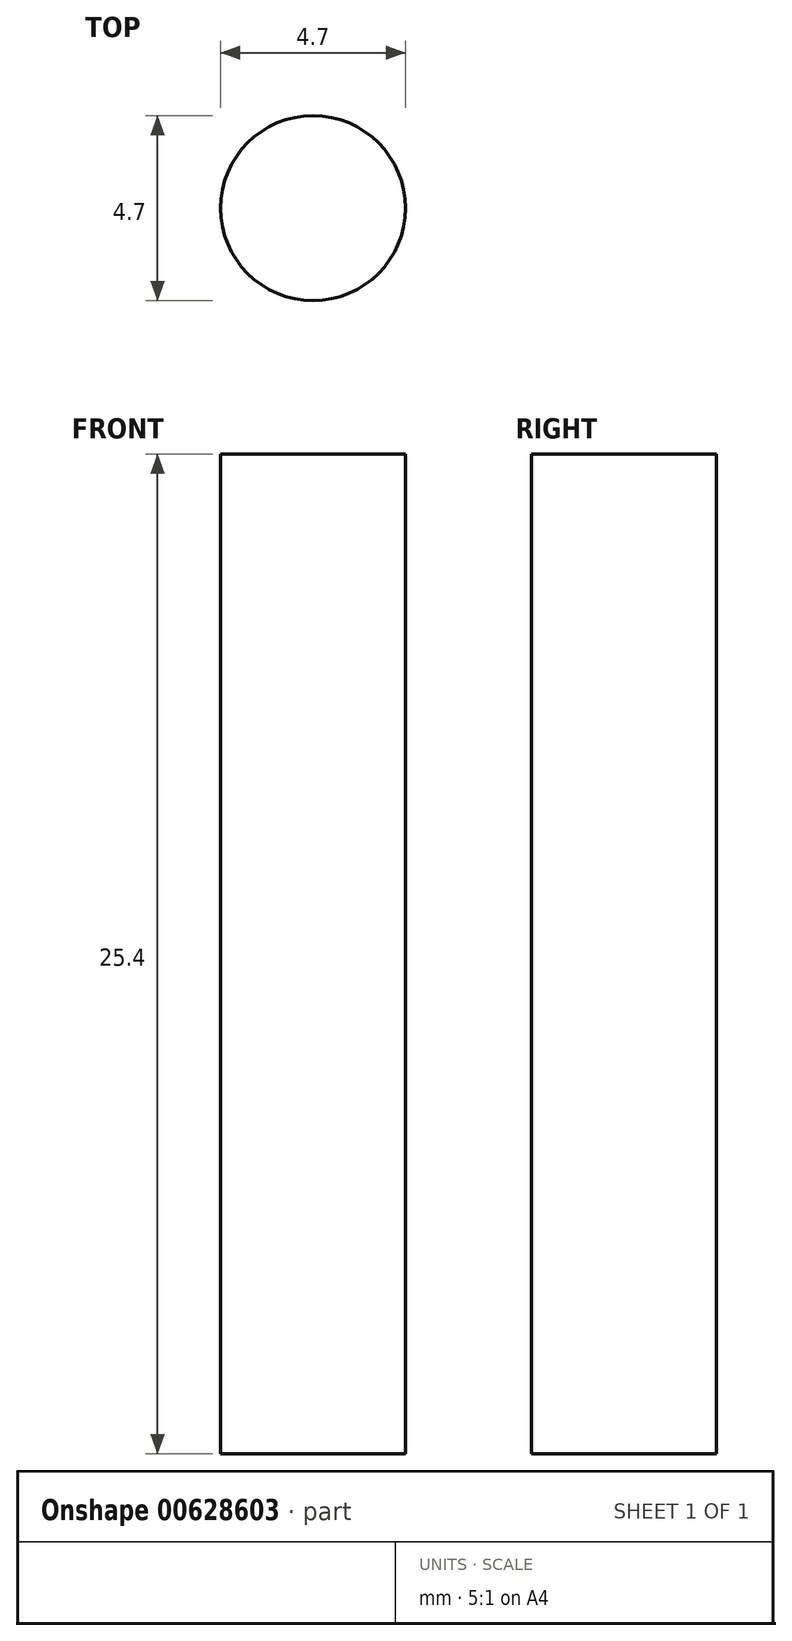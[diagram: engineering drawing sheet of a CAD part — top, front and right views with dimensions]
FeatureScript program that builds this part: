
annotation { "Feature Type Name" : "Feature", "Feature Type Description" : "" }
export const myFeature = defineFeature(function(context is Context, id is Id, definition is map)
    precondition{}
    {
        {
            var Q0;
            Q0=qCreatedBy(makeId("Top.planeOp"),FACE);
            var sketch = newSketch(context, id + "F0", { "sketchPlane" : qUnion([Q0])});
            skCircle(sketch, "E0", {"center": v(0, 0) * mm, "radius": 2.35 * mm});
            skSolve(sketch);
        }
        {
            var Q0;
            Q0=makeQuery(id+"F0.imprint","IMPRINT",FACE,{"disambiguationData":[TD([[makeQuery(id+"F0.imprint","IMPRINT",EDGE,{"derivedFrom":sQuery(id+"F0.wireOp",EDGE,"E0")}),1.0]])]});
            extrude(context, id + "F1", {"entities" : qUnion([Q0]), "depth" : 25.4 * mm, "offsetDistance" : 25.4 * mm});
        }
    });
